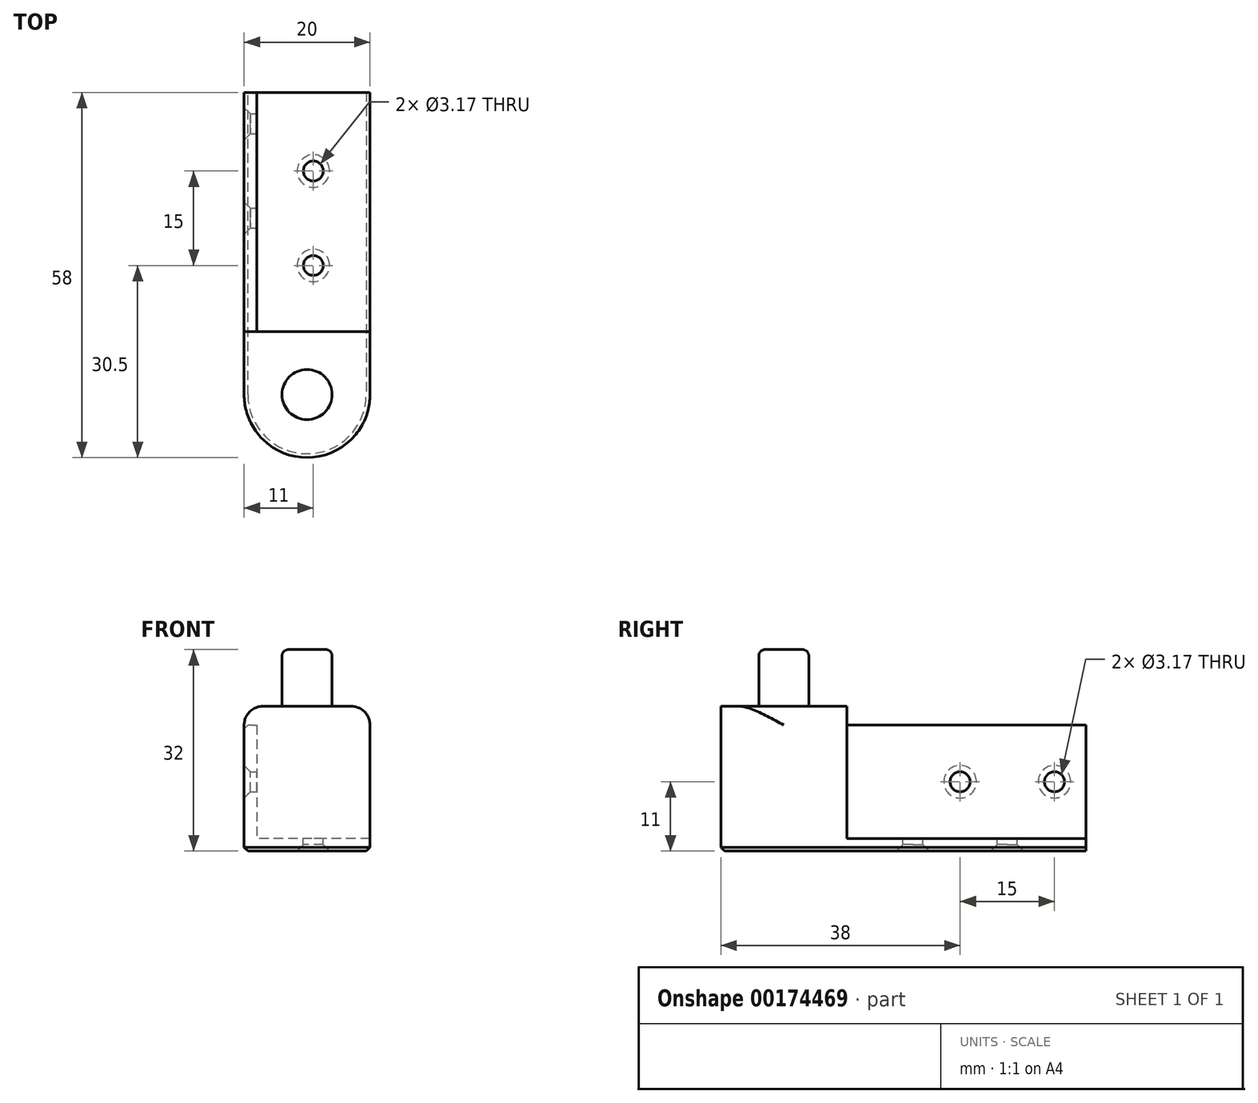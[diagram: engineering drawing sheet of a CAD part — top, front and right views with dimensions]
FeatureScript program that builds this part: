
annotation { "Feature Type Name" : "Feature", "Feature Type Description" : "" }
export const myFeature = defineFeature(function(context is Context, id is Id, definition is map)
    precondition{}
    {
        {
            var Q0;
            Q0=qCreatedBy(makeId("Front.planeOp"),FACE);
            var sketch = newSketch(context, id + "F0", { "sketchPlane" : qUnion([Q0])});
            skLineSegment(sketch, "E0", {"start": v(-2, -2) * mm, "end": v(-2, 18) * mm});
            skLineSegment(sketch, "E1", {"start": v(-2, 18) * mm, "end": v(0, 18) * mm});
            skLineSegment(sketch, "E2", {"start": v(-2, -2) * mm, "end": v(18, -2) * mm});
            skLineSegment(sketch, "E3", {"start": v(0, 18) * mm, "end": v(0, 0) * mm});
            skLineSegment(sketch, "E4", {"start": v(0, 0) * mm, "end": v(18, 0) * mm});
            skLineSegment(sketch, "E5", {"start": v(18, 0) * mm, "end": v(18, -2) * mm});
            skSolve(sketch);
        }
        {
            var Q0;
            Q0=makeQuery(id+"F0.imprint","IMPRINT",FACE,{"disambiguationData":[TD([[makeQuery(id+"F0.imprint","IMPRINT",EDGE,{"derivedFrom":sQuery(id+"F0.wireOp",EDGE,"E0")}),-1.0]])]});
            extrude(context, id + "F1", {"entities" : qUnion([Q0]), "oppositeDirection" : true, "depth" : 40 * mm});
        }
        {
            var Q0;
            Q0=makeQuery(id+"F1.opExtrude","SWEPT_FACE",FACE,{"disambiguationData":[OSD([sQuery(id+"F0.wireOp",EDGE,"BLrCOVyg-vFY3-6Uj6-42PL-0wbM1FOnHA4J"),sQuery(id+"F0.wireOp",EDGE,"E3")])]});
            var sketch = newSketch(context, id + "F2", { "sketchPlane" : qUnion([Q0])});
            skLineSegment(sketch, "E6.bottom", {"start": v(0, 18) * mm, "end": v(2, 18) * mm});
            skLineSegment(sketch, "E6.top", {"start": v(0, 0) * mm, "end": v(2, 0) * mm});
            skLineSegment(sketch, "E6.left", {"start": v(0, 18) * mm, "end": v(0, 0) * mm});
            skLineSegment(sketch, "E6.right", {"start": v(2, 18) * mm, "end": v(2, 0) * mm});
            skSolve(sketch);
        }
        {
            var Q0;
            Q0=qSketchRegion(id+"F2",true);
            var Q1;
            Q1=makeQuery(id+"F1.opExtrude","SWEPT_FACE",FACE,{"disambiguationData":[OSD([sQuery(id+"F0.wireOp",EDGE,"E5")])]});
            extrude(context, id + "F3", {"entities" : qUnion([Q0]), "operationType" : NewBodyOperationType.ADD, "endBound" : BoundingType.UP_TO_SURFACE, "endBoundEntityFace" : qUnion([Q1]), "depth" : 25 * mm});
        }
        {
            var Q0;
            Q0=makeQuery(id+"F1.opExtrude","SWEPT_FACE",FACE,{"disambiguationData":[OSD([sQuery(id+"F0.wireOp",EDGE,"E4")])]});
            var sketch = newSketch(context, id + "F4", { "sketchPlane" : qUnion([Q0])});
            skLineSegment(sketch, "E7", {"start": v(9, 40) * mm, "end": v(9, 27.5) * mm, "construction": true});
            skLineSegment(sketch, "E8", {"start": v(9, 27.5) * mm, "end": v(9, 12.5) * mm, "construction": true});
            skCircle(sketch, "E9", {"center": v(9, 27.5) * mm, "radius": 1.59 * mm});
            skCircle(sketch, "E10", {"center": v(9, 12.5) * mm, "radius": 1.59 * mm});
            skSolve(sketch);
        }
        {
            var Q0;
            Q0=makeQuery(id+"F4.imprint","IMPRINT",FACE,{"disambiguationData":[TD([[makeQuery(id+"F4.imprint","IMPRINT",EDGE,{"derivedFrom":sQuery(id+"F4.wireOp",EDGE,"E10")}),1.0]])]});
            var Q1;
            Q1=makeQuery(id+"F4.imprint","IMPRINT",FACE,{"disambiguationData":[TD([[makeQuery(id+"F4.imprint","IMPRINT",EDGE,{"derivedFrom":sQuery(id+"F4.wireOp",EDGE,"E9")}),1.0]])]});
            extrude(context, id + "F5", {"entities" : qUnion([Q0, Q1]), "operationType" : NewBodyOperationType.REMOVE, "endBound" : BoundingType.THROUGH_ALL, "oppositeDirection" : true, "depth" : 25 * mm});
        }
        {
            var Q0;
            Q0=makeQuery(id+"F1.opExtrude","SWEPT_FACE",FACE,{"disambiguationData":[OSD([sQuery(id+"F0.wireOp",EDGE,"E3")])]});
            var sketch = newSketch(context, id + "F6", { "sketchPlane" : qUnion([Q0])});
            skLineSegment(sketch, "E11", {"start": v(40, 9) * mm, "end": v(35, 9) * mm, "construction": true});
            skLineSegment(sketch, "E12", {"start": v(35, 9) * mm, "end": v(20, 9) * mm, "construction": true});
            skCircle(sketch, "E13", {"center": v(35, 9) * mm, "radius": 1.59 * mm});
            skCircle(sketch, "E14", {"center": v(20, 9) * mm, "radius": 1.59 * mm});
            skSolve(sketch);
        }
        {
            var Q0;
            Q0=qSketchRegion(id+"F6",true);
            extrude(context, id + "F7", {"entities" : qUnion([Q0]), "operationType" : NewBodyOperationType.REMOVE, "endBound" : BoundingType.THROUGH_ALL, "oppositeDirection" : true, "depth" : 25 * mm});
        }
        {
            var Q0;
            Q0=makeQuery(id+"F7.boolean.opBoolean","INTERSECT",EDGE,{"derivedFrom":[makeQuery(id+"F1.opExtrude","SWEPT_FACE",FACE,{"disambiguationData":[OSD([sQuery(id+"F0.wireOp",EDGE,"E0")])]}),makeQuery(id+"F7.opExtrude","SWEPT_FACE",FACE,{"disambiguationData":[OSD([sQuery(id+"F6.wireOp",EDGE,"E14")])]})]});
            var Q1;
            Q1=makeQuery(id+"F7.boolean.opBoolean","INTERSECT",EDGE,{"derivedFrom":[makeQuery(id+"F1.opExtrude","SWEPT_FACE",FACE,{"disambiguationData":[OSD([sQuery(id+"F0.wireOp",EDGE,"E0")])]}),makeQuery(id+"F7.opExtrude","SWEPT_FACE",FACE,{"disambiguationData":[OSD([sQuery(id+"F6.wireOp",EDGE,"E13")])]})]});
            var Q2;
            Q2=makeQuery(id+"F5.boolean.opBoolean","INTERSECT",EDGE,{"derivedFrom":[makeQuery(id+"F1.opExtrude","SWEPT_FACE",FACE,{"disambiguationData":[OSD([sQuery(id+"F0.wireOp",EDGE,"E2")])]}),makeQuery(id+"F5.opExtrude","SWEPT_FACE",FACE,{"disambiguationData":[OSD([sQuery(id+"F4.wireOp",EDGE,"E9")])]})]});
            var Q3;
            Q3=makeQuery(id+"F5.boolean.opBoolean","INTERSECT",EDGE,{"derivedFrom":[makeQuery(id+"F1.opExtrude","SWEPT_FACE",FACE,{"disambiguationData":[OSD([sQuery(id+"F0.wireOp",EDGE,"E2")])]}),makeQuery(id+"F5.opExtrude","SWEPT_FACE",FACE,{"disambiguationData":[OSD([sQuery(id+"F4.wireOp",EDGE,"E10")])]})]});
            chamfer(context, id + "F8", {"entities" : qUnion([Q0, Q1, Q2, Q3]), "width" : 1 * mm, "tangentPropagation" : true});
        }
        {
            var Q0;
            Q0=makeQuery(id+"F3.boolean.opBoolean","MERGE",FACE,{"derivedFrom":[makeQuery(id+"F1.opExtrude","SWEPT_FACE",FACE,{"disambiguationData":[OSD([sQuery(id+"F0.wireOp",EDGE,"E1")])]}),makeQuery(id+"F3.opExtrude","SWEPT_FACE",FACE,{"disambiguationData":[OSD([sQuery(id+"F2.wireOp",EDGE,"E6.bottom")])]})]});
            var sketch = newSketch(context, id + "F9", { "sketchPlane" : qUnion([Q0])});
            skLineSegment(sketch, "E15.bottom", {"start": v(18, 2) * mm, "end": v(-2, 2) * mm});
            skLineSegment(sketch, "E15.top", {"start": v(18, -18) * mm, "end": v(-2, -18) * mm});
            skLineSegment(sketch, "E15.left", {"start": v(18, 2) * mm, "end": v(18, -18) * mm});
            skLineSegment(sketch, "E15.right", {"start": v(-2, 2) * mm, "end": v(-2, -18) * mm});
            skSolve(sketch);
        }
        {
            var Q0;
            {var subQ0=sQuery(id+"F9.wireOp",EDGE,"E15.top");Q0=makeQuery(id+"F9.imprint","IMPRINT",FACE,{"disambiguationData":[TD([[makeQuery(id+"F9.imprint","IMPRINT",EDGE,{"derivedFrom":subQ0}),-1.0]])]});}
            var Q1;
            Q1=makeQuery(id+"F1.opExtrude","SWEPT_FACE",FACE,{"disambiguationData":[OSD([sQuery(id+"F0.wireOp",EDGE,"E2")])]});
            extrude(context, id + "F10", {"entities" : qUnion([Q0]), "operationType" : NewBodyOperationType.ADD, "endBound" : BoundingType.UP_TO_SURFACE, "oppositeDirection" : true, "endBoundEntityFace" : qUnion([Q1]), "depth" : 25 * mm});
        }
        {
            var Q0;
            {var subQ0=sQuery(id+"F2.wireOp",EDGE,"E6.bottom");var subQ1=sQuery(id+"F0.wireOp",EDGE,"E1");Q0=makeQuery(id+"F10.boolean.opBoolean","MERGE",FACE,{"derivedFrom":[makeQuery(id+"F3.boolean.opBoolean","MERGE",FACE,{"derivedFrom":[makeQuery(id+"F1.opExtrude","SWEPT_FACE",FACE,{"disambiguationData":[OSD([subQ1])]}),makeQuery(id+"F3.opExtrude","SWEPT_FACE",FACE,{"disambiguationData":[OSD([subQ0])]})]}),makeQuery(id+"F10.opExtrude","CAP_FACE",FACE,{"disambiguationData":[OSD([subQ1,subQ0,sQuery(id+"F2.wireOp",EDGE,"E6.left"),sQuery(id+"F9.wireOp",EDGE,"E15.top"),sQuery(id+"F9.wireOp",EDGE,"E15.left"),sQuery(id+"F9.wireOp",EDGE,"E15.right")])],"isStart":true})]});}
            var sketch = newSketch(context, id + "F11", { "sketchPlane" : qUnion([Q0])});
            skLineSegment(sketch, "E16.bottom", {"start": v(18, 2) * mm, "end": v(-2, 2) * mm});
            skLineSegment(sketch, "E16.top", {"start": v(18, -18) * mm, "end": v(-2, -18) * mm});
            skLineSegment(sketch, "E16.left", {"start": v(18, 2) * mm, "end": v(18, -18) * mm});
            skLineSegment(sketch, "E16.right", {"start": v(-2, 2) * mm, "end": v(-2, -18) * mm});
            skSolve(sketch);
        }
        {
            var Q0;
            Q0=makeQuery(id+"F11.imprint","IMPRINT",FACE,{"disambiguationData":[TD([[makeQuery(id+"F11.imprint","IMPRINT",EDGE,{"derivedFrom":sQuery(id+"F11.wireOp",EDGE,"E16.top")}),-1.0]])]});
            extrude(context, id + "F12", {"entities" : qUnion([Q0]), "operationType" : NewBodyOperationType.ADD, "depth" : 3 * mm});
        }
        {
            var Q0;
            Q0=makeQuery(id+"F12.opExtrude","CAP_FACE",FACE,{"disambiguationData":[OSD([sQuery(id+"F11.wireOp",EDGE,"E16.bottom"),sQuery(id+"F11.wireOp",EDGE,"E16.top"),sQuery(id+"F11.wireOp",EDGE,"E16.left"),sQuery(id+"F11.wireOp",EDGE,"E16.right")])],"isStart":false});
            var sketch = newSketch(context, id + "F13", { "sketchPlane" : qUnion([Q0])});
            skLineSegment(sketch, "E17", {"start": v(18, 2) * mm, "end": v(-2, -18) * mm, "construction": true});
            skCircle(sketch, "E18", {"center": v(8, -8) * mm, "radius": 3.98 * mm});
            skSolve(sketch);
        }
        {
            var Q0;
            Q0=makeQuery(id+"F13.imprint","IMPRINT",FACE,{"disambiguationData":[TD([[makeQuery(id+"F13.imprint","IMPRINT",EDGE,{"derivedFrom":sQuery(id+"F13.wireOp",EDGE,"E18")}),1.0]])]});
            var Q1;
            Q1=sQuery(id+"F13.wireOp",EDGE,"E18");
            extrude(context, id + "F14", {"entities" : qUnion([Q0]), "operationType" : NewBodyOperationType.ADD, "surfaceEntities" : qUnion([Q1]), "depth" : 9 * mm});
        }
        {
            var Q0;
            Q0=makeQuery(id+"F14.opExtrude","CAP_EDGE",EDGE,{"disambiguationData":[OSD([sQuery(id+"F13.wireOp",EDGE,"E18")])],"isStart":false});
            fillet(context, id + "F15", {"entities" : qUnion([Q0]), "radius" : 1 * mm, "tangentPropagation" : true, "allowEdgeOverflow" : false});
        }
        {
            var Q0;
            Q0=makeQuery(id+"F12.boolean.opBoolean","MERGE",EDGE,{"derivedFrom":[makeQuery(id+"F10.opExtrude","SWEPT_EDGE",EDGE,{"disambiguationData":[OSD([sQuery(id+"F9.wireOp",EDGE,"E15.top"),sQuery(id+"F9.wireOp",EDGE,"E15.right")])]}),makeQuery(id+"F12.opExtrude","SWEPT_EDGE",EDGE,{"disambiguationData":[OSD([sQuery(id+"F11.wireOp",EDGE,"E16.top"),sQuery(id+"F11.wireOp",EDGE,"E16.right")])]})]});
            var Q1;
            Q1=makeQuery(id+"F12.boolean.opBoolean","MERGE",EDGE,{"derivedFrom":[makeQuery(id+"F10.opExtrude","SWEPT_EDGE",EDGE,{"disambiguationData":[OSD([sQuery(id+"F9.wireOp",EDGE,"E15.top"),sQuery(id+"F9.wireOp",EDGE,"E15.left")])]}),makeQuery(id+"F12.opExtrude","SWEPT_EDGE",EDGE,{"disambiguationData":[OSD([sQuery(id+"F11.wireOp",EDGE,"E16.top"),sQuery(id+"F11.wireOp",EDGE,"E16.left")])]})]});
            fillet(context, id + "F16", {"entities" : qUnion([Q0, Q1]), "radius" : 10 * mm, "tangentPropagation" : true, "allowEdgeOverflow" : false});
        }
        {
            var Q0;
            {var subQ0=sQuery(id+"F11.wireOp",EDGE,"E16.right");var subQ1=sQuery(id+"F11.wireOp",EDGE,"E16.top");Q0=makeQuery(id+"F16.opFillet","BLEND_EDGE",EDGE,{"blendedFrom":[makeQuery(id+"F12.boolean.opBoolean","MERGE",EDGE,{"derivedFrom":[makeQuery(id+"F10.opExtrude","SWEPT_EDGE",EDGE,{"disambiguationData":[OSD([sQuery(id+"F9.wireOp",EDGE,"E15.top"),sQuery(id+"F9.wireOp",EDGE,"E15.right")])]}),makeQuery(id+"F12.opExtrude","SWEPT_EDGE",EDGE,{"disambiguationData":[OSD([subQ1,subQ0])]})]}),makeQuery(id+"F12.opExtrude","CAP_FACE",FACE,{"disambiguationData":[OSD([sQuery(id+"F11.wireOp",EDGE,"E16.bottom"),subQ1,sQuery(id+"F11.wireOp",EDGE,"E16.left"),subQ0])],"isStart":false})],"blendedInto":[makeQuery(id+"F12.opExtrude","CAP_FACE",FACE,{"disambiguationData":[OSD([sQuery(id+"F11.wireOp",EDGE,"E16.bottom"),subQ1,sQuery(id+"F11.wireOp",EDGE,"E16.left"),subQ0])],"isStart":false})]});}
            var Q1;
            Q1=makeQuery(id+"F12.opExtrude","CAP_EDGE",EDGE,{"disambiguationData":[OSD([sQuery(id+"F11.wireOp",EDGE,"E16.right")])],"isStart":false});
            var Q2;
            Q2=makeQuery(id+"F12.opExtrude","CAP_EDGE",EDGE,{"disambiguationData":[OSD([sQuery(id+"F11.wireOp",EDGE,"E16.left")])],"isStart":false});
            fillet(context, id + "F17", {"entities" : qUnion([Q0, Q1, Q2]), "radius" : 3 * mm, "allowEdgeOverflow" : false});
        }
        {
            var Q0;
            Q0=makeQuery(id+"F10.boolean.opBoolean","MERGE",EDGE,{"derivedFrom":[makeQuery(id+"F1.opExtrude","SWEPT_EDGE",EDGE,{"disambiguationData":[OSD([sQuery(id+"F0.wireOp",EDGE,"E0"),sQuery(id+"F0.wireOp",EDGE,"E1")])]}),makeQuery(id+"F10.opExtrude","CAP_EDGE",EDGE,{"disambiguationData":[OSD([sQuery(id+"F9.wireOp",EDGE,"E15.right")])],"isStart":true})]});
            fillet(context, id + "F18", {"entities" : qUnion([Q0]), "radius" : 1 * mm, "tangentPropagation" : true, "allowEdgeOverflow" : false});
        }
        {
            var Q0;
            {var subQ0=sQuery(id+"F9.wireOp",EDGE,"E15.left");var subQ1=sQuery(id+"F0.wireOp",EDGE,"E2");Q0=makeQuery(id+"F10.boolean.opBoolean","MERGE",EDGE,{"derivedFrom":[makeQuery(id+"F1.opExtrude","SWEPT_EDGE",EDGE,{"disambiguationData":[OSD([subQ1,sQuery(id+"F0.wireOp",EDGE,"E5")])]}),makeQuery(id+"F10.opExtrude","TWEAK_EDGE",EDGE,{"derivedFrom":[makeQuery(id+"F1.opExtrude","SWEPT_FACE",FACE,{"disambiguationData":[OSD([subQ1])]}),makeQuery(id+"F9.imprint","IMPRINT",EDGE,{"disambiguationData":[TD([[makeQuery(id+"F9.imprint","INTERSECT",VERTEX,{"derivedFrom":[sQuery(id+"F9.wireOp",EDGE,"E15.top"),subQ0]}),1.0]])],"derivedFrom":subQ0})]})]});}
            chamfer(context, id + "F19", {"entities" : qUnion([Q0]), "width" : 0.6 * mm, "tangentPropagation" : true});
        }
    });
